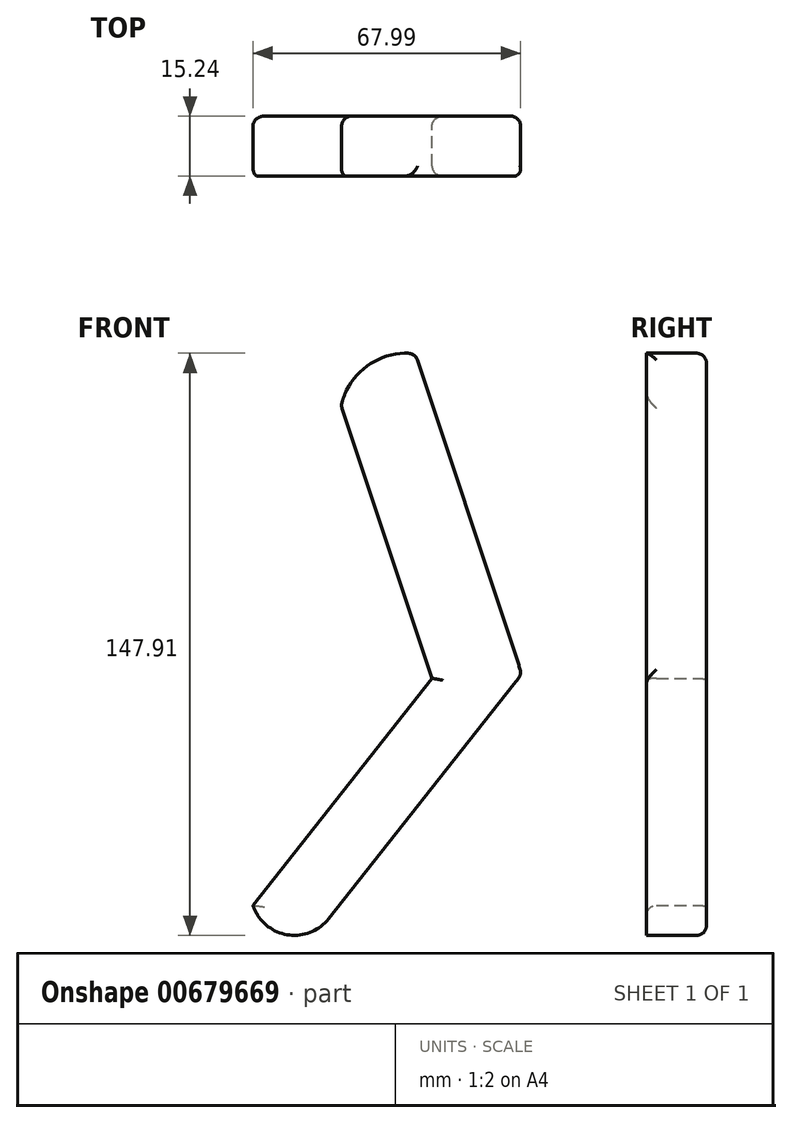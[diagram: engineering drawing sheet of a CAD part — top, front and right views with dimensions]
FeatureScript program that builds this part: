
annotation { "Feature Type Name" : "Feature", "Feature Type Description" : "" }
export const myFeature = defineFeature(function(context is Context, id is Id, definition is map)
    precondition{}
    {
        {
            var Q0;
            Q0=qCreatedBy(makeId("Front.planeOp"),FACE);
            var sketch = newSketch(context, id + "F0", { "sketchPlane" : qUnion([Q0])});
            skLineSegment(sketch, "E0", {"start": v(3.23, 57.94) * mm, "end": v(27.92, -16.2) * mm});
            skLineSegment(sketch, "E1", {"start": v(-15.61, 44.78) * mm, "end": v(7.46, -24.49) * mm});
            skArc(sketch, "E2", {"start": v(30.21, -23.49) * mm, "mid": v(18.58, -18.12) * mm, "end": v(7.46, -24.49) * mm});
            skArc(sketch, "E3", {"start": v(30.21, -23.49) * mm, "mid": v(29.1, -19.84) * mm, "end": v(27.92, -16.2) * mm});
            skArc(sketch, "E4", {"start": v(3.23, 57.94) * mm, "mid": v(-8.77, 55.04) * mm, "end": v(-15.61, 44.78) * mm});
            skLineSegment(sketch, "E5", {"start": v(7.46, -24.49) * mm, "end": v(-38.04, -82.13) * mm});
            skLineSegment(sketch, "E6", {"start": v(30.21, -23.49) * mm, "end": v(-18.82, -85.6) * mm});
            skArc(sketch, "E7", {"start": v(-38.04, -82.13) * mm, "mid": v(-29.47, -89.64) * mm, "end": v(-18.82, -85.6) * mm});
            skSolve(sketch);
        }
        {
            var Q0;
            Q0=makeQuery(id+"F0.imprint","IMPRINT",FACE,{"disambiguationData":[TD([[makeQuery(id+"F0.imprint","IMPRINT",EDGE,{"derivedFrom":sQuery(id+"F0.wireOp",EDGE,"E0")}),-1.0]])]});
            extrude(context, id + "F1", {"entities" : qUnion([Q0]), "depth" : 15.24 * mm, "offsetDistance" : 25.4 * mm});
        }
        {
            var Q0;
            Q0=makeQuery(id+"F0.imprint","IMPRINT",FACE,{"disambiguationData":[TD([[makeQuery(id+"F0.imprint","IMPRINT",EDGE,{"derivedFrom":sQuery(id+"F0.wireOp",EDGE,"E0")}),-1.0]])]});
            var Q1;
            Q1=makeQuery(id+"F0.imprint","IMPRINT",FACE,{"disambiguationData":[TD([[makeQuery(id+"F0.imprint","IMPRINT",EDGE,{"derivedFrom":sQuery(id+"F0.wireOp",EDGE,"E2")}),1.0]])]});
            extrude(context, id + "F2", {"entities" : qUnion([Q0, Q1]), "operationType" : NewBodyOperationType.ADD, "depth" : 15.24 * mm, "offsetDistance" : 25.4 * mm});
        }
        {
            var Q0;
            Q0=makeQuery(id+"F1.opExtrude","CAP_EDGE",EDGE,{"disambiguationData":[OSD([sQuery(id+"F0.wireOp",EDGE,"E0")])],"isStart":false});
            var Q1;
            Q1=makeQuery(id+"F1.opExtrude","CAP_EDGE",EDGE,{"disambiguationData":[OSD([sQuery(id+"F0.wireOp",EDGE,"E0")])],"isStart":true});
            var Q2;
            Q2=makeQuery(id+"F1.opExtrude","CAP_EDGE",EDGE,{"disambiguationData":[OSD([sQuery(id+"F0.wireOp",EDGE,"E1")])],"isStart":true});
            var Q3;
            Q3=makeQuery(id+"F1.opExtrude","CAP_EDGE",EDGE,{"disambiguationData":[OSD([sQuery(id+"F0.wireOp",EDGE,"E1")])],"isStart":false});
            var Q4;
            Q4=makeQuery(id+"F2.opExtrude","CAP_EDGE",EDGE,{"disambiguationData":[OSD([sQuery(id+"F0.wireOp",EDGE,"E5")])],"isStart":true});
            var Q5;
            Q5=makeQuery(id+"F2.opExtrude","CAP_EDGE",EDGE,{"disambiguationData":[OSD([sQuery(id+"F0.wireOp",EDGE,"E5")])],"isStart":false});
            var Q6;
            Q6=makeQuery(id+"F1.opExtrude","CAP_EDGE",EDGE,{"disambiguationData":[OSD([sQuery(id+"F0.wireOp",EDGE,"E4")])],"isStart":true});
            var Q7;
            Q7=makeQuery(id+"F1.opExtrude","SWEPT_EDGE",EDGE,{"disambiguationData":[OSD([sQuery(id+"F0.wireOp",EDGE,"E0"),sQuery(id+"F0.wireOp",EDGE,"E4")])]});
            var Q8;
            Q8=makeQuery(id+"F1.opExtrude","SWEPT_EDGE",EDGE,{"disambiguationData":[OSD([sQuery(id+"F0.wireOp",EDGE,"E1"),sQuery(id+"F0.wireOp",EDGE,"E4")])]});
            var Q9;
            Q9=makeQuery(id+"F2.opExtrude","CAP_EDGE",EDGE,{"disambiguationData":[OSD([sQuery(id+"F0.wireOp",EDGE,"E6")])],"isStart":true});
            var Q10;
            {var subQ0=sQuery(id+"F0.wireOp",EDGE,"E6");var subQ1=sQuery(id+"F0.wireOp",EDGE,"E3");var subQ2=sQuery(id+"F0.wireOp",EDGE,"E2");Q10=makeQuery(id+"F2.boolean.opBoolean","MERGE",EDGE,{"derivedFrom":[makeQuery(id+"F1.opExtrude","SWEPT_EDGE",EDGE,{"disambiguationData":[OSD([subQ2,subQ1,subQ0])]}),makeQuery(id+"F2.opExtrude","SWEPT_EDGE",EDGE,{"disambiguationData":[OSD([subQ2,subQ1,subQ0])]})]});}
            fillet(context, id + "F3", {"entities" : qUnion([Q0, Q1, Q2, Q3, Q4, Q5, Q6, Q7, Q8, Q9, Q10]), "radius" : 2.54 * mm, "tangentPropagation" : true, "allowEdgeOverflow" : false});
        }
    });
